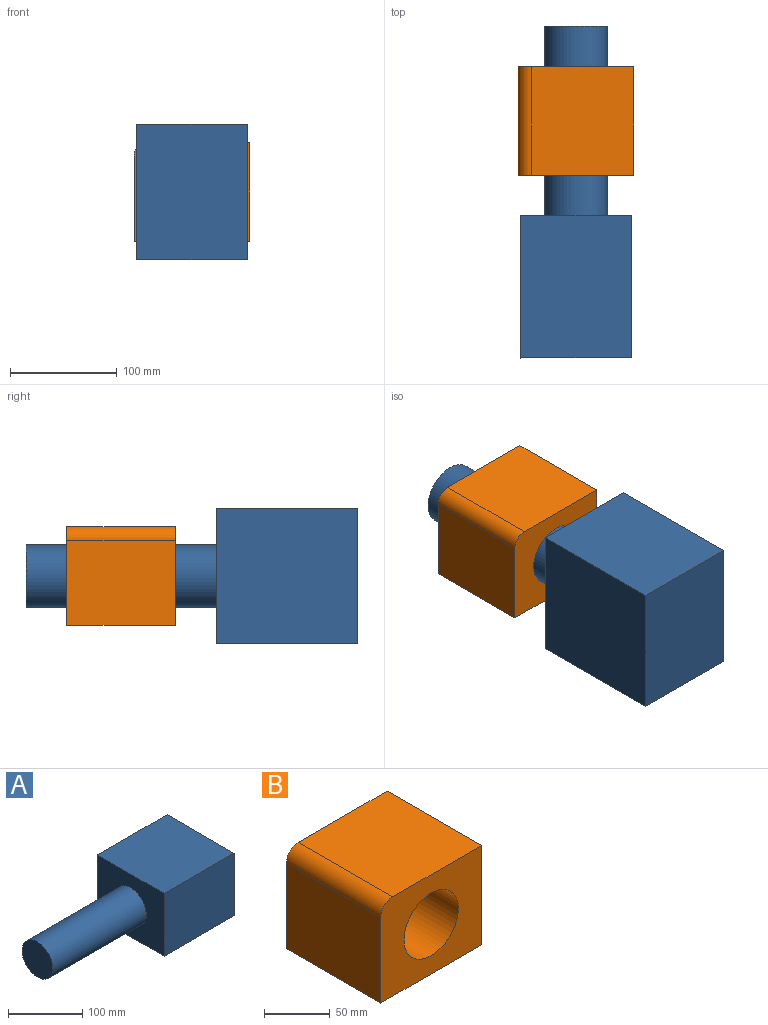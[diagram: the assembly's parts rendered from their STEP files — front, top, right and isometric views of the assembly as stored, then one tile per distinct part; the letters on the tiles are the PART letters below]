
ASSEMBLY  parts=2 mates=1
PART A: 8 faces, bbox 310.5x127x103.3 mm
  f0: plane 132.69x127mm, normal (0,0,1), area 16851.1mm2, adj f1,f3,f4,f5
  f1: plane 127x103.26mm, normal (-1,0,0), area 10433.9mm2, adj f0,f2,f4,f5,f6
  f2: plane 132.69x127mm, normal (0,0,-1), area 16851.1mm2, adj f1,f3,f4,f5
  f3: plane 127x103.26mm, normal (1,0,0), area 13114.4mm2, adj f0,f2,f4,f5
  f4: plane 132.69x103.26mm, normal (0,-1,0), area 13701.5mm2, adj f0,f1,f2,f3
  f5: plane 132.69x103.26mm, normal (0,1,0), area 13701.5mm2, adj f0,f1,f2,f3
  f6: cylinder r=29.21mm len=177.8mm, axis (1,0,0), area 32632mm2, adj f1,f7
  f7: plane 58.42x58.42mm, normal (-1,0,0), area 2680.5mm2, adj f6
PART B: 8 faces, bbox 108.4x101.6x92.5 mm
  f0: plane 101.6x95.75mm, normal (0,0,1), area 9728.1mm2, adj f3,f4,f5,f7
  f1: plane 101.6x79.83mm, normal (-1,0,0), area 8110.9mm2, adj f2,f4,f5,f7
  f2: plane 108.45x101.6mm, normal (0,0,-1), area 11018.4mm2, adj f1,f3,f4,f5
  f3: plane 101.6x92.53mm, normal (1,0,0), area 9401.2mm2, adj f0,f2,f4,f5
  f4: plane 108.45x92.53mm, normal (0,-1,0), area 7319.8mm2, adj f0,f1,f2,f3,f6,f7
  f5: plane 108.45x92.53mm, normal (0,1,0), area 7319.8mm2, adj f0,f1,f2,f3,f6,f7
  f6: cylinder r=29.21mm len=101.6mm, axis (0,-1,0), area 18646.8mm2, adj f4,f5
  f7: cylinder r=12.7mm len=101.6mm, axis (0,-1,0), area 2026.8mm2, adj f0,f1,f4,f5
PLACE A rot(axis=(-0.58,0.58,-0.58),120deg) t=(126.47,-234.21,190.14)mm fixed
PLACE B rot(axis=(0.08,0.93,0.35),0deg) t=(126.47,-78.97,190.14)mm
MATE pin_slot A.f6 <-> B.f6  axis (0,-1,0) through (126.47,9.93,190.14)mm
